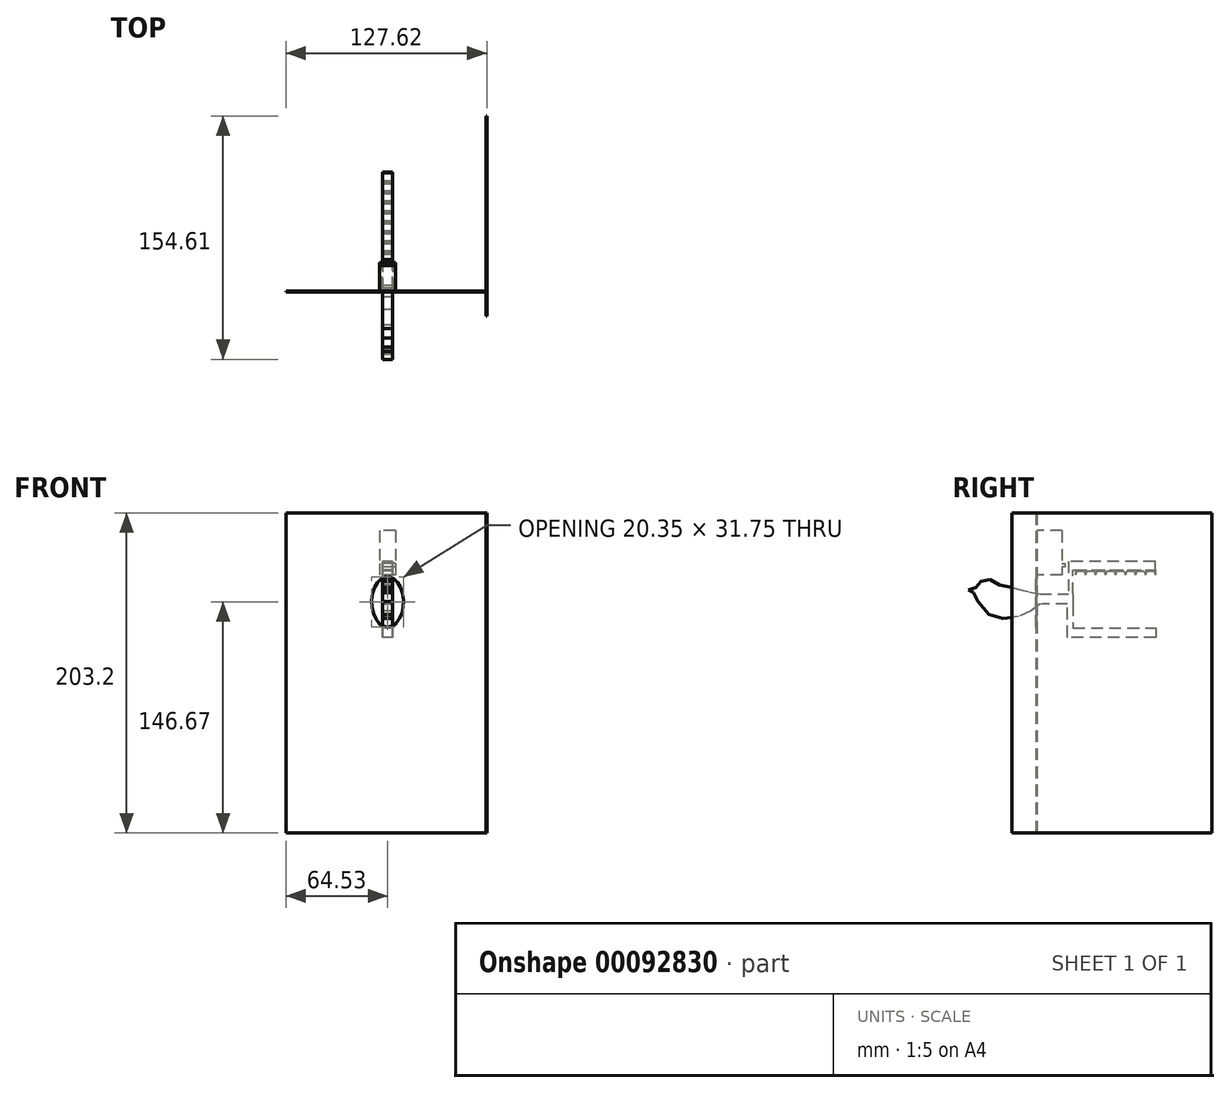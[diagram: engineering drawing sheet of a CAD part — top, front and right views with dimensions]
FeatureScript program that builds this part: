
annotation { "Feature Type Name" : "Feature", "Feature Type Description" : "" }
export const myFeature = defineFeature(function(context is Context, id is Id, definition is map)
    precondition{}
    {
        {
            assignVariable(context, id + "F0", {"name" : "BoardWidth", "anyValue" : .625});
        }
        {
            var Q0;
            Q0=qCreatedBy(makeId("Right.planeOp"),FACE);
            var sketch = newSketch(context, id + "F1", { "sketchPlane" : qUnion([Q0])});
            skLineSegment(sketch, "E0", {"start": v(-43.5, 39.45) * mm, "end": v(-38.6, 41.06) * mm});
            skLineSegment(sketch, "E1", {"start": v(-35.6, 44.91) * mm, "end": v(-38.6, 41.06) * mm});
            skLineSegment(sketch, "E2", {"start": v(-35.6, 44.91) * mm, "end": v(-29.87, 46.02) * mm});
            skLineSegment(sketch, "E3", {"start": v(-29.87, 46.02) * mm, "end": v(-23.71, 42.69) * mm});
            skLineSegment(sketch, "E4", {"start": v(-23.71, 42.69) * mm, "end": v(1.83, 36.67) * mm});
            skLineSegment(sketch, "E5", {"start": v(1.83, 36.67) * mm, "end": v(19.92, 36.67) * mm});
            skLineSegment(sketch, "E6", {"start": v(19.5, 30.38) * mm, "end": v(3.44, 30.38) * mm});
            skLineSegment(sketch, "E7", {"start": v(3.44, 30.38) * mm, "end": v(1.56, 30.11) * mm});
            skLineSegment(sketch, "E8", {"start": v(1.56, 30.11) * mm, "end": v(-3.87, 26) * mm});
            skLineSegment(sketch, "E9", {"start": v(-3.87, 26) * mm, "end": v(-11.65, 22.42) * mm});
            skLineSegment(sketch, "E10", {"start": v(-11.65, 22.42) * mm, "end": v(-21.49, 21.13) * mm});
            skLineSegment(sketch, "E11", {"start": v(-21.49, 21.13) * mm, "end": v(-30.38, 23.77) * mm});
            skLineSegment(sketch, "E12", {"start": v(-30.38, 23.77) * mm, "end": v(-37.48, 31.91) * mm});
            skLineSegment(sketch, "E13", {"start": v(-37.48, 31.91) * mm, "end": v(-40.3, 37.73) * mm});
            skLineSegment(sketch, "E14", {"start": v(-40.3, 37.73) * mm, "end": v(-43.5, 39.45) * mm});
            skLineSegment(sketch, "E15", {"start": v(-29.87, 46.02) * mm, "end": v(-29.87, 21.13) * mm, "construction": true});
            skLineSegment(sketch, "E16", {"start": v(-29.87, 33.58) * mm, "end": v(50, 33.58) * mm, "construction": true});
            skLineSegment(sketch, "E17", {"start": v(22.98, 30.38) * mm, "end": v(22.98, 15.12) * mm});
            skLineSegment(sketch, "E18", {"start": v(23.01, 36.67) * mm, "end": v(23.01, 51.92) * mm});
            skLineSegment(sketch, "E19", {"start": v(23.01, 51.92) * mm, "end": v(75.23, 51.92) * mm});
            skLineSegment(sketch, "E20", {"start": v(75.23, 51.92) * mm, "end": v(75.23, 57.6) * mm});
            skLineSegment(sketch, "E21", {"start": v(75.23, 57.6) * mm, "end": v(19.92, 57.6) * mm});
            skLineSegment(sketch, "E22", {"start": v(19.92, 57.6) * mm, "end": v(19.92, 36.67) * mm});
            skLineSegment(sketch, "E23", {"start": v(22.98, 15.12) * mm, "end": v(75.54, 15.12) * mm});
            skLineSegment(sketch, "E24", {"start": v(75.54, 15.12) * mm, "end": v(75.54, 9.27) * mm});
            skLineSegment(sketch, "E25", {"start": v(75.54, 9.27) * mm, "end": v(19.5, 9.27) * mm});
            skLineSegment(sketch, "E26", {"start": v(19.5, 9.27) * mm, "end": v(19.5, 30.38) * mm});
            skLineSegment(sketch, "E27", {"start": v(23.01, 36.67) * mm, "end": v(22.98, 30.38) * mm});
            skSolve(sketch);
        }
        {
            var Q0;
            Q0=qSketchRegion(id+"F1",true);
            extrude(context, id + "F2", {"entities" : qUnion([Q0]), "depth" : 3.17 * mm, "hasSecondDirection" : true, "secondDirectionOppositeDirection" : true, "secondDirectionDepth" : 3.17 * mm});
        }
        {
            var Q0;
            Q0=qCreatedBy(makeId("Front.planeOp"),FACE);
            var sketch = newSketch(context, id + "F3", { "sketchPlane" : qUnion([Q0])});
            skLineSegment(sketch, "E28.bottom", {"start": v(-64.53, 88.28) * mm, "end": v(62.47, 88.28) * mm});
            skLineSegment(sketch, "E28.top", {"start": v(-64.53, -114.92) * mm, "end": v(62.47, -114.92) * mm});
            skLineSegment(sketch, "E28.left", {"start": v(-64.53, 88.28) * mm, "end": v(-64.53, -114.92) * mm});
            skLineSegment(sketch, "E28.right", {"start": v(62.47, 88.28) * mm, "end": v(62.47, -114.92) * mm});
            skEllipse(sketch, "E29", {"center": v(0, 31.75) * mm, "majorRadius": 15.88 * mm, "minorRadius": 10.18 * mm, "majorAxis": v(0, -1)});
            skSolve(sketch);
        }
        {
            var Q0;
            Q0=qSketchRegion(id+"F3",true);
            extrude(context, id + "F4", {"entities" : qUnion([Q0]), "depth" : (getVariable(context, 'BoardWidth')) * mm});
        }
        {
            var Q0;
            Q0=makeQuery(id+"F4.opExtrude","SWEPT_FACE",FACE,{"disambiguationData":[OSD([sQuery(id+"F3.wireOp",EDGE,"E28.right")])]});
            var sketch = newSketch(context, id + "F5", { "sketchPlane" : qUnion([Q0])});
            skLineSegment(sketch, "E30.bottom", {"start": v(-15.88, 88.28) * mm, "end": v(111.12, 88.28) * mm});
            skLineSegment(sketch, "E30.top", {"start": v(-15.88, -114.92) * mm, "end": v(111.12, -114.92) * mm});
            skLineSegment(sketch, "E30.left", {"start": v(-15.88, 88.28) * mm, "end": v(-15.88, -114.92) * mm});
            skLineSegment(sketch, "E30.right", {"start": v(111.12, 88.28) * mm, "end": v(111.12, -114.92) * mm});
            skSolve(sketch);
        }
        {
            var Q0;
            Q0=qSketchRegion(id+"F5",true);
            extrude(context, id + "F6", {"entities" : qUnion([Q0]), "depth" : (getVariable(context, 'BoardWidth')) * mm});
        }
        {
            var Q0;
            Q0=qCreatedBy(makeId("Right.planeOp"),FACE);
            var sketch = newSketch(context, id + "F7", { "sketchPlane" : qUnion([Q0])});
            skLineSegment(sketch, "E31.bottom", {"start": v(16, 77.05) * mm, "end": v(0, 77.05) * mm});
            skLineSegment(sketch, "E31.top", {"start": v(16, 49.05) * mm, "end": v(0, 49.05) * mm});
            skLineSegment(sketch, "E31.left", {"start": v(16, 77.05) * mm, "end": v(16, 49.05) * mm});
            skLineSegment(sketch, "E31.right", {"start": v(0, 77.05) * mm, "end": v(0, 49.05) * mm});
            skLineSegment(sketch, "E32", {"start": v(16, 56.2) * mm, "end": v(17.93, 56.2) * mm});
            skLineSegment(sketch, "E33", {"start": v(17.93, 56.2) * mm, "end": v(17.93, 54.1) * mm});
            skLineSegment(sketch, "E34", {"start": v(17.93, 54.1) * mm, "end": v(16, 54.1) * mm});
            skSolve(sketch);
        }
        {
            var Q0;
            Q0=qSketchRegion(id+"F7",true);
            extrude(context, id + "F8", {"entities" : qUnion([Q0]), "depth" : 5.1 * mm, "hasSecondDirection" : true, "secondDirectionOppositeDirection" : true, "secondDirectionDepth" : 5.1 * mm});
        }
        {
            var Q0;
            Q0=makeQuery(id+"F2.opExtrude","CAP_FACE",FACE,{"disambiguationData":[OSD([sQuery(id+"F1.wireOp",EDGE,"E0"),sQuery(id+"F1.wireOp",EDGE,"E1"),sQuery(id+"F1.wireOp",EDGE,"E2"),sQuery(id+"F1.wireOp",EDGE,"E3"),sQuery(id+"F1.wireOp",EDGE,"E4"),sQuery(id+"F1.wireOp",EDGE,"E5"),sQuery(id+"F1.wireOp",EDGE,"E6"),sQuery(id+"F1.wireOp",EDGE,"E7"),sQuery(id+"F1.wireOp",EDGE,"E8"),sQuery(id+"F1.wireOp",EDGE,"E9"),sQuery(id+"F1.wireOp",EDGE,"E10"),sQuery(id+"F1.wireOp",EDGE,"E11"),sQuery(id+"F1.wireOp",EDGE,"E12"),sQuery(id+"F1.wireOp",EDGE,"E13"),sQuery(id+"F1.wireOp",EDGE,"E14"),sQuery(id+"F1.wireOp",EDGE,"E17"),sQuery(id+"F1.wireOp",EDGE,"E18"),sQuery(id+"F1.wireOp",EDGE,"E19"),sQuery(id+"F1.wireOp",EDGE,"E20"),sQuery(id+"F1.wireOp",EDGE,"E21"),sQuery(id+"F1.wireOp",EDGE,"E22"),sQuery(id+"F1.wireOp",EDGE,"E23"),sQuery(id+"F1.wireOp",EDGE,"E24"),sQuery(id+"F1.wireOp",EDGE,"E25"),sQuery(id+"F1.wireOp",EDGE,"E26"),sQuery(id+"F1.wireOp",EDGE,"E27")])],"isStart":true});
            var sketch = newSketch(context, id + "F9", { "sketchPlane" : qUnion([Q0])});
            skLineSegment(sketch, "E35", {"start": v(-75.23, 51.92) * mm, "end": v(-68.88, 51.92) * mm, "construction": true});
            skLineSegment(sketch, "E36", {"start": v(-75.23, 51.92) * mm, "end": v(-75.23, 51.28) * mm});
            skLineSegment(sketch, "E37", {"start": v(-69.8, 51.28) * mm, "end": v(-74.3, 51.28) * mm});
            skLineSegment(sketch, "E38", {"start": v(-68.88, 51.92) * mm, "end": v(-68.88, 51.28) * mm});
            skLineSegment(sketch, "E39", {"start": v(-75.23, 51.92) * mm, "end": v(-68.88, 51.92) * mm});
            skLineSegment(sketch, "E40", {"start": v(-74.3, 51.28) * mm, "end": v(-75.23, 48.74) * mm});
            skLineSegment(sketch, "E41", {"start": v(-69.8, 51.28) * mm, "end": v(-68.88, 48.74) * mm});
            skLineSegment(sketch, "E42", {"start": v(-75.23, 51.28) * mm, "end": v(-75.23, 48.74) * mm});
            skLineSegment(sketch, "E43", {"start": v(-68.88, 51.28) * mm, "end": v(-68.88, 48.74) * mm});
            skLineSegment(sketch, "E44.1.0.0", {"start": v(-63.46, 51.28) * mm, "end": v(-62.53, 48.74) * mm});
            skLineSegment(sketch, "E44.1.0.1", {"start": v(-63.46, 51.28) * mm, "end": v(-67.96, 51.28) * mm});
            skLineSegment(sketch, "E44.1.0.2", {"start": v(-67.96, 51.28) * mm, "end": v(-68.88, 48.74) * mm});
            skLineSegment(sketch, "E44.1.0.4", {"start": v(-62.53, 51.28) * mm, "end": v(-62.53, 48.74) * mm});
            skLineSegment(sketch, "E44.1.0.5", {"start": v(-68.88, 51.92) * mm, "end": v(-62.53, 51.92) * mm});
            skLineSegment(sketch, "E44.1.0.6", {"start": v(-68.88, 51.92) * mm, "end": v(-62.53, 51.92) * mm, "construction": true});
            skLineSegment(sketch, "E44.1.0.8", {"start": v(-62.53, 51.92) * mm, "end": v(-62.53, 51.28) * mm});
            skLineSegment(sketch, "E44.2.0.0", {"start": v(-57.1, 51.28) * mm, "end": v(-56.18, 48.74) * mm});
            skLineSegment(sketch, "E44.2.0.1", {"start": v(-57.1, 51.28) * mm, "end": v(-61.6, 51.28) * mm});
            skLineSegment(sketch, "E44.2.0.2", {"start": v(-61.6, 51.28) * mm, "end": v(-62.53, 48.74) * mm});
            skLineSegment(sketch, "E44.2.0.3", {"start": v(-62.53, 51.28) * mm, "end": v(-62.53, 48.74) * mm});
            skLineSegment(sketch, "E44.2.0.4", {"start": v(-56.18, 51.28) * mm, "end": v(-56.18, 48.74) * mm});
            skLineSegment(sketch, "E44.2.0.5", {"start": v(-62.53, 51.92) * mm, "end": v(-56.18, 51.92) * mm});
            skLineSegment(sketch, "E44.2.0.6", {"start": v(-62.53, 51.92) * mm, "end": v(-56.18, 51.92) * mm, "construction": true});
            skLineSegment(sketch, "E44.2.0.7", {"start": v(-62.53, 51.92) * mm, "end": v(-62.53, 51.28) * mm});
            skLineSegment(sketch, "E44.2.0.8", {"start": v(-56.18, 51.92) * mm, "end": v(-56.18, 51.28) * mm});
            skLineSegment(sketch, "E44.3.0.0", {"start": v(-50.76, 51.28) * mm, "end": v(-49.83, 48.74) * mm});
            skLineSegment(sketch, "E44.3.0.1", {"start": v(-50.76, 51.28) * mm, "end": v(-55.26, 51.28) * mm});
            skLineSegment(sketch, "E44.3.0.2", {"start": v(-55.26, 51.28) * mm, "end": v(-56.18, 48.74) * mm});
            skLineSegment(sketch, "E44.3.0.3", {"start": v(-56.18, 51.28) * mm, "end": v(-56.18, 48.74) * mm});
            skLineSegment(sketch, "E44.3.0.4", {"start": v(-49.83, 51.28) * mm, "end": v(-49.83, 48.74) * mm});
            skLineSegment(sketch, "E44.3.0.5", {"start": v(-56.18, 51.92) * mm, "end": v(-49.83, 51.92) * mm});
            skLineSegment(sketch, "E44.3.0.6", {"start": v(-56.18, 51.92) * mm, "end": v(-49.83, 51.92) * mm, "construction": true});
            skLineSegment(sketch, "E44.3.0.7", {"start": v(-56.18, 51.92) * mm, "end": v(-56.18, 51.28) * mm});
            skLineSegment(sketch, "E44.3.0.8", {"start": v(-49.83, 51.92) * mm, "end": v(-49.83, 51.28) * mm});
            skLineSegment(sketch, "E44.4.0.0", {"start": v(-44.4, 51.28) * mm, "end": v(-43.48, 48.74) * mm});
            skLineSegment(sketch, "E44.4.0.1", {"start": v(-44.4, 51.28) * mm, "end": v(-48.9, 51.28) * mm});
            skLineSegment(sketch, "E44.4.0.2", {"start": v(-48.9, 51.28) * mm, "end": v(-49.83, 48.74) * mm});
            skLineSegment(sketch, "E44.4.0.3", {"start": v(-49.83, 51.28) * mm, "end": v(-49.83, 48.74) * mm});
            skLineSegment(sketch, "E44.4.0.4", {"start": v(-43.48, 51.28) * mm, "end": v(-43.48, 48.74) * mm});
            skLineSegment(sketch, "E44.4.0.5", {"start": v(-49.83, 51.92) * mm, "end": v(-43.48, 51.92) * mm});
            skLineSegment(sketch, "E44.4.0.6", {"start": v(-49.83, 51.92) * mm, "end": v(-43.48, 51.92) * mm, "construction": true});
            skLineSegment(sketch, "E44.4.0.7", {"start": v(-49.83, 51.92) * mm, "end": v(-49.83, 51.28) * mm});
            skLineSegment(sketch, "E44.4.0.8", {"start": v(-43.48, 51.92) * mm, "end": v(-43.48, 51.28) * mm});
            skLineSegment(sketch, "E44.5.0.0", {"start": v(-38.06, 51.28) * mm, "end": v(-37.13, 48.74) * mm});
            skLineSegment(sketch, "E44.5.0.1", {"start": v(-38.06, 51.28) * mm, "end": v(-42.56, 51.28) * mm});
            skLineSegment(sketch, "E44.5.0.2", {"start": v(-42.56, 51.28) * mm, "end": v(-43.48, 48.74) * mm});
            skLineSegment(sketch, "E44.5.0.3", {"start": v(-43.48, 51.28) * mm, "end": v(-43.48, 48.74) * mm});
            skLineSegment(sketch, "E44.5.0.4", {"start": v(-37.13, 51.28) * mm, "end": v(-37.13, 48.74) * mm});
            skLineSegment(sketch, "E44.5.0.5", {"start": v(-43.48, 51.92) * mm, "end": v(-37.13, 51.92) * mm});
            skLineSegment(sketch, "E44.5.0.6", {"start": v(-43.48, 51.92) * mm, "end": v(-37.13, 51.92) * mm, "construction": true});
            skLineSegment(sketch, "E44.5.0.7", {"start": v(-43.48, 51.92) * mm, "end": v(-43.48, 51.28) * mm});
            skLineSegment(sketch, "E44.5.0.8", {"start": v(-37.13, 51.92) * mm, "end": v(-37.13, 51.28) * mm});
            skLineSegment(sketch, "E44.6.0.0", {"start": v(-31.7, 51.28) * mm, "end": v(-30.78, 48.74) * mm});
            skLineSegment(sketch, "E44.6.0.1", {"start": v(-31.7, 51.28) * mm, "end": v(-36.2, 51.28) * mm});
            skLineSegment(sketch, "E44.6.0.2", {"start": v(-36.2, 51.28) * mm, "end": v(-37.13, 48.74) * mm});
            skLineSegment(sketch, "E44.6.0.3", {"start": v(-37.13, 51.28) * mm, "end": v(-37.13, 48.74) * mm});
            skLineSegment(sketch, "E44.6.0.4", {"start": v(-30.78, 51.28) * mm, "end": v(-30.78, 48.74) * mm});
            skLineSegment(sketch, "E44.6.0.5", {"start": v(-37.13, 51.92) * mm, "end": v(-30.78, 51.92) * mm});
            skLineSegment(sketch, "E44.6.0.6", {"start": v(-37.13, 51.92) * mm, "end": v(-30.78, 51.92) * mm, "construction": true});
            skLineSegment(sketch, "E44.6.0.7", {"start": v(-37.13, 51.92) * mm, "end": v(-37.13, 51.28) * mm});
            skLineSegment(sketch, "E44.6.0.8", {"start": v(-30.78, 51.92) * mm, "end": v(-30.78, 51.28) * mm});
            skLineSegment(sketch, "E44.7.0.0", {"start": v(-25.36, 51.28) * mm, "end": v(-24.43, 48.74) * mm});
            skLineSegment(sketch, "E44.7.0.1", {"start": v(-25.36, 51.28) * mm, "end": v(-29.86, 51.28) * mm});
            skLineSegment(sketch, "E44.7.0.2", {"start": v(-29.86, 51.28) * mm, "end": v(-30.78, 48.74) * mm});
            skLineSegment(sketch, "E44.7.0.3", {"start": v(-30.78, 51.28) * mm, "end": v(-30.78, 48.74) * mm});
            skLineSegment(sketch, "E44.7.0.4", {"start": v(-24.43, 51.28) * mm, "end": v(-24.43, 48.74) * mm});
            skLineSegment(sketch, "E44.7.0.5", {"start": v(-30.78, 51.92) * mm, "end": v(-24.43, 51.92) * mm});
            skLineSegment(sketch, "E44.7.0.6", {"start": v(-30.78, 51.92) * mm, "end": v(-24.43, 51.92) * mm, "construction": true});
            skLineSegment(sketch, "E44.7.0.7", {"start": v(-30.78, 51.92) * mm, "end": v(-30.78, 51.28) * mm});
            skLineSegment(sketch, "E44.7.0.8", {"start": v(-24.43, 51.92) * mm, "end": v(-24.43, 51.28) * mm});
            skLineSegment(sketch, "E44.direction1", {"start": v(-68.88, 48.74) * mm, "end": v(-62.53, 48.74) * mm, "construction": true});
            skSolve(sketch);
        }
        {
            var Q0;
            Q0 = qSketchRegion(id + "F9", true);
            extrude(context, id + "F10", {"entities" : qUnion([Q0]), "oppositeDirection" : true, "depth" : 6.35 * mm});
        }
    });
